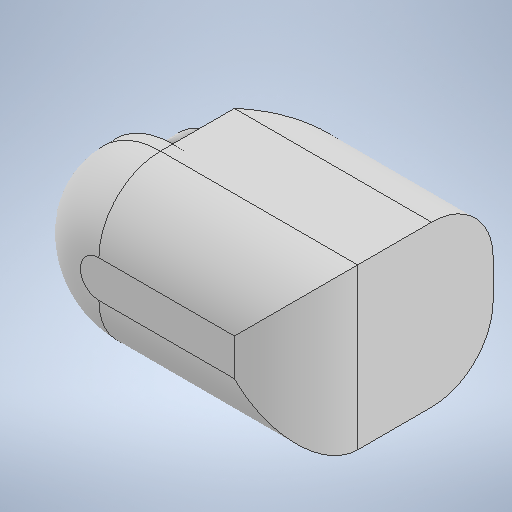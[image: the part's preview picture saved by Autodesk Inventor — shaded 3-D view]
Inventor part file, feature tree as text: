
AUTODESK INVENTOR PART (.ipt)
format: ipt  version: 2025.2 (Build 292293000, 293)  size: 245,248 bytes
history: native  units: mm
features: extrude x3, other x1, sketch x1, fillet x1
ambient origin geometry x8: Origin, YZ Plane, XZ Plane, XY Plane, X Axis, Y Axis, Z Axis, Center Point
bodies: Body1 (feature_tree)
feature tree (6):
  other  "Bryła1"
  sketch  "Szkic1"
  extrude  "Wyciągnięcie proste1"  Depth=20.0mm
  extrude  "Wyciągnięcie proste2"  Depth=26.0mm
  extrude  "Wyciągnięcie proste3"  Depth=4.9mm
  fillet  "Zaokrąglenie1"  Radius=8.0mm
